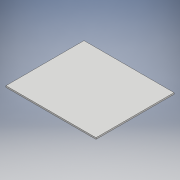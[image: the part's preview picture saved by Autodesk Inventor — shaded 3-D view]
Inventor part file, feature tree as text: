
AUTODESK INVENTOR PART (.ipt)
format: ipt  version: 2017 (Build 210142000, 142)  size: 93,696 bytes
history: native  units: mm
features: sheet_metal_op x1, sketch x1, other x1
ambient origin geometry x8: Origin, YZ Plane, XZ Plane, XY Plane, X Axis, Y Axis, Z Axis, Center Point
bodies: Solid1 (feature_tree)
feature tree (3):
  sheet_metal_op  "Face1"
  sketch  "Sketch1"  dims[d0=30.0mm d1=26.0mm d2=0.5mm]
  other  "Plate1"
